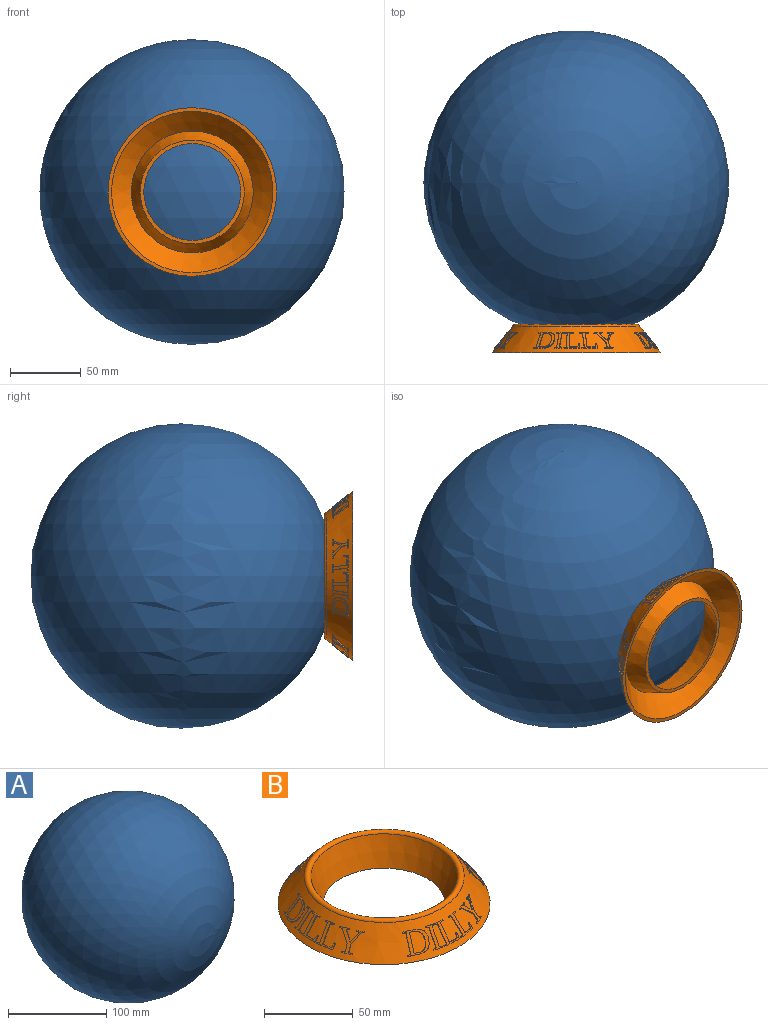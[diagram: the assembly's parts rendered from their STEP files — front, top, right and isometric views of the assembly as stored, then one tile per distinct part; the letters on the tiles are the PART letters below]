
ASSEMBLY  parts=2 mates=1
PART A: 1 faces, bbox 215.9x215.9x215.9 mm
  f0: sphere r=107.95mm, area 146438.5mm2
PART B: 359 faces, bbox 119.7x119.7x20.4 mm
  f0: cone r=34.29mm half-angle=20.4deg, axis (0,0,1), area 4748.7mm2, adj f1,f6
  f1: torus R=43.18mm, axis (0,0,1), area 1338.6mm2, adj f0,f2
  f2: cone r=45.08mm half-angle=37.9deg, axis (0,0,-1), area 6513.8mm2, adj f1,f3,f14,f15,f16,f17,f18,f19
  f3: plane 119.38x119.38mm, normal (0,0,-1), area 932.3mm2, adj f2,f4
  f4: cone r=57.15mm half-angle=44.5deg, axis (0,0,-1), area 6284.1mm2, adj f3,f5
  f5: cone r=36.83mm half-angle=24.1deg, axis (0,0,1), area 3915.4mm2, adj f4,f6
  f6: plane 73.66x73.66mm, normal (0,0,-1), area 567.5mm2, adj f0,f5
  f7: extruded ~4.03x1.55mm, area 2.2mm2, adj f8,f13,f26,f27
  f8: extruded ~4.07x2.56mm, area 2.5mm2, adj f7,f9,f26,f27
  f9: extruded ~3.88x3.58mm, area 2.5mm2, adj f8,f10,f26,f27
  f10: extruded ~3.93x3.1mm, area 2.5mm2, adj f9,f11,f26,f27
  f11: plane 1.87x1.21mm, normal (-0.56,0.25,-0.79), area 1mm2, adj f10,f12,f26,f27
  f12: plane 9.9x7.21mm, normal (-0.41,-0.91,0), area 6.2mm2, adj f11,f13,f26,f27
  f13: extruded ~2.9x1.7mm, area 1.5mm2, adj f7,f12,f26,f27
  f14: plane 1.69x1.4mm, normal (-0.49,0.38,-0.78), area 0.9mm2, adj f2,f15,f25,f26
  f15: plane 10.12x7.39mm, normal (0.41,0.91,0), area 6.3mm2, adj f2,f14,f16,f26
  f16: plane 1.84x1.07mm, normal (0.62,-0.11,0.78), area 0.9mm2, adj f2,f15,f17,f26
  f17: plane 0.75x0.68mm, normal (0.41,0.91,0), area 0.3mm2, adj f2,f16,f18,f26
  f18: plane 1.77x1.23mm, normal (-0.56,0.25,-0.79), area 0.9mm2, adj f2,f17,f19,f26
  f19: plane 4.72x2.66mm, normal (-0.56,0.26,-0.79), area 2.5mm2, adj f2,f18,f20,f26
  f20: extruded ~5.6x1.84mm, area 3mm2, adj f2,f19,f21,f26
  f21: extruded ~4.62x3.21mm, area 2.9mm2, adj f2,f20,f22,f26
  f22: extruded ~4.52x4.16mm, area 2.9mm2, adj f2,f21,f23,f26
  f23: extruded ~5.04x3.83mm, area 3.1mm2, adj f2,f22,f24,f26
  f24: plane 5.98x3.42mm, normal (0.56,-0.25,0.79), area 3.3mm2, adj f2,f23,f25,f26
  f25: plane 0.75x0.68mm, normal (0.41,0.91,0), area 0.3mm2, adj f2,f14,f24,f26
  f26: cone r=45.48mm half-angle=37.9deg, axis (0,0,-1), area 71mm2, adj f7,f8,f9,f10,f11,f12,f13,f14
  f27: cone r=45.08mm half-angle=37.9deg, axis (0,0,-1), area 86.4mm2, adj f7,f8,f9,f10,f11,f12,f13
  f28: plane 0.75x0.73mm, normal (-0.22,-0.98,0), area 0.3mm2, adj f2,f29,f39,f40
  f29: plane 5.66x1.75mm, normal (0.6,-0.14,0.79), area 2.9mm2, adj f2,f28,f30,f40
  f30: plane 0.75x0.73mm, normal (0.22,0.98,0), area 0.3mm2, adj f2,f29,f31,f40
  f31: plane 1.81x1.01mm, normal (-0.56,0.28,-0.78), area 0.9mm2, adj f2,f30,f32,f40
  f32: plane 10.09x7.83mm, normal (0.22,0.98,0), area 6.3mm2, adj f2,f31,f33,f40
  f33: plane 1.89x0.67mm, normal (0.63,0.02,0.78), area 0.9mm2, adj f2,f32,f34,f40
  f34: plane 0.75x0.73mm, normal (0.22,0.98,0), area 0.3mm2, adj f2,f33,f35,f40
  f35: plane 5.65x1.73mm, normal (-0.6,0.14,-0.79), area 2.9mm2, adj f2,f34,f36,f40
  f36: plane 0.75x0.73mm, normal (-0.22,-0.98,0), area 0.3mm2, adj f2,f35,f37,f40
  f37: plane 1.82x0.94mm, normal (0.56,-0.28,0.78), area 0.9mm2, adj f2,f36,f38,f40
  f38: plane 10.09x7.82mm, normal (-0.22,-0.98,0), area 6.3mm2, adj f2,f37,f39,f40
  f39: plane 1.9x0.6mm, normal (-0.63,-0.01,-0.78), area 0.9mm2, adj f2,f28,f38,f40
  f40: cone r=45.48mm half-angle=37.9deg, axis (0,0,-1), area 33.3mm2, adj f28,f29,f30,f31,f32,f33,f34,f35
  f41: plane 6.11x1.03mm, normal (0.61,-0.03,0.79), area 3.1mm2, adj f2,f42,f55,f56
  f42: plane 0.75x0.74mm, normal (-0.05,-1,0), area 0.3mm2, adj f2,f41,f43,f56
  f43: plane 2.21x0.56mm, normal (-0.62,-0.09,-0.78), area 1.1mm2, adj f2,f42,f44,f56
  f44: plane 10.05x7.99mm, normal (-0.05,-1,0), area 6.3mm2, adj f2,f43,f45,f56
  f45: plane 2.8x0.58mm, normal (0.61,-0.03,0.79), area 1.4mm2, adj f2,f44,f46,f56
  f46: extruded ~3.3x0.54mm, area 1.7mm2, adj f2,f45,f47,f56
  f47: plane 2.61x2.21mm, normal (0.18,0.97,0.17), area 1.5mm2, adj f2,f46,f48,f56
  f48: plane 0.7x0.41mm, normal (0.61,-0.03,0.79), area 0.3mm2, adj f2,f47,f49,f56
  f49: plane 3.49x2.9mm, normal (-0.08,-1,-0.04), area 2.1mm2, adj f2,f48,f50,f56
  f50: plane 11.34x1.31mm, normal (-0.61,0.03,-0.79), area 5.6mm2, adj f2,f49,f51,f56
  f51: plane 0.75x0.74mm, normal (0.05,1,0), area 0.3mm2, adj f2,f50,f52,f56
  f52: plane 1.83x0.62mm, normal (0.61,0.12,0.78), area 0.9mm2, adj f2,f51,f53,f56
  f53: plane 10.11x8.06mm, normal (0.05,1,0), area 6.3mm2, adj f2,f52,f54,f56
  f54: plane 1.82x0.78mm, normal (-0.6,0.18,-0.78), area 0.9mm2, adj f2,f53,f55,f56
  f55: plane 0.75x0.75mm, normal (0.05,1,0), area 0.3mm2, adj f2,f41,f54,f56
  f56: cone r=45.48mm half-angle=37.9deg, axis (0,0,-1), area 43.3mm2, adj f41,f42,f43,f44,f45,f46,f47,f48
  f57: plane 0.75x0.74mm, normal (-0.17,0.99,0), area 0.3mm2, adj f2,f58,f71,f72
  f58: plane 1.91x0.45mm, normal (-0.62,0.04,-0.78), area 0.9mm2, adj f2,f57,f59,f72
  f59: plane 10.11x7.95mm, normal (-0.17,0.99,0), area 6.3mm2, adj f2,f58,f60,f72
  f60: plane 1.84x0.79mm, normal (0.57,0.26,0.78), area 0.9mm2, adj f2,f59,f61,f72
  f61: plane 0.75x0.73mm, normal (-0.17,0.99,0), area 0.3mm2, adj f2,f60,f62,f72
  f62: plane 11.26x2.56mm, normal (-0.61,-0.11,-0.79), area 5.6mm2, adj f2,f61,f63,f72
  f63: plane 3.49x2.9mm, normal (0.14,-0.99,-0.04), area 2.1mm2, adj f2,f62,f64,f72
  f64: plane 0.73x0.55mm, normal (0.61,0.11,0.79), area 0.3mm2, adj f2,f63,f65,f72
  f65: plane 2.61x2.32mm, normal (-0.04,0.98,0.17), area 1.5mm2, adj f2,f64,f66,f72
  f66: extruded ~3.29x1.16mm, area 1.7mm2, adj f2,f65,f67,f72
  f67: plane 2.82x0.87mm, normal (0.61,0.11,0.79), area 1.4mm2, adj f2,f66,f68,f72
  f68: plane 10.05x7.88mm, normal (0.17,-0.99,0), area 6.3mm2, adj f2,f67,f69,f72
  f69: plane 2.2x0.92mm, normal (-0.58,-0.23,-0.78), area 1.1mm2, adj f2,f68,f70,f72
  f70: plane 0.75x0.73mm, normal (0.17,-0.99,0), area 0.3mm2, adj f2,f69,f71,f72
  f71: plane 6.13x1.31mm, normal (0.61,0.11,0.79), area 3.1mm2, adj f2,f57,f70,f72
  f72: cone r=45.48mm half-angle=37.9deg, axis (0,0,-1), area 43.3mm2, adj f57,f58,f59,f60,f61,f62,f63,f64
  f73: plane 0.75x0.68mm, normal (0.41,-0.91,0), area 0.3mm2, adj f2,f74,f93,f94
  f74: plane 4.29x2.53mm, normal (0.56,0.25,0.79), area 2.3mm2, adj f2,f73,f75,f94
  f75: plane 0.75x0.68mm, normal (-0.41,0.91,0), area 0.3mm2, adj f2,f74,f76,f94
  f76: plane 1.84x1.01mm, normal (-0.62,-0.11,-0.78), area 0.9mm2, adj f2,f75,f77,f94
  f77: plane 5.83x5.52mm, normal (-0.06,0.91,0.4), area 3.8mm2, adj f2,f76,f78,f94
  f78: plane 5.68x5.53mm, normal (0.64,-0.64,0.42), area 3.9mm2, adj f2,f77,f79,f94
  f79: plane 1.86x1.24mm, normal (-0.5,-0.38,-0.78), area 1mm2, adj f2,f78,f80,f94
  f80: plane 0.75x0.68mm, normal (0.41,-0.91,0), area 0.3mm2, adj f2,f79,f81,f94
  f81: plane 5.86x2.56mm, normal (0.56,0.25,0.79), area 3mm2, adj f2,f80,f82,f94
  f82: plane 0.75x0.68mm, normal (-0.41,0.91,0), area 0.3mm2, adj f2,f81,f83,f94
  f83: plane 1.74x0.74mm, normal (-0.62,-0.09,-0.78), area 0.8mm2, adj f2,f82,f84,f94
  f84: plane 6.97x6.5mm, normal (-0.64,0.64,-0.42), area 4.7mm2, adj f2,f83,f85,f94
  f85: plane 3.97x2.97mm, normal (-0.41,0.91,0), area 2.4mm2, adj f2,f84,f86,f94
  f86: plane 2.17x1.39mm, normal (0.51,0.36,0.78), area 1.1mm2, adj f2,f85,f87,f94
  f87: plane 0.75x0.68mm, normal (-0.41,0.91,0), area 0.3mm2, adj f2,f86,f88,f94
  f88: plane 6.21x3.09mm, normal (-0.56,-0.25,-0.79), area 3.3mm2, adj f2,f87,f89,f94
  f89: plane 0.75x0.68mm, normal (0.41,-0.91,0), area 0.3mm2, adj f2,f88,f90,f94
  f90: plane 2.27x1.17mm, normal (0.61,0.13,0.78), area 1.1mm2, adj f2,f89,f91,f94
  f91: plane 4.02x3mm, normal (0.41,-0.91,0), area 2.4mm2, adj f2,f90,f92,f94
  f92: plane 6.97x6.49mm, normal (0.06,-0.91,-0.41), area 4.6mm2, adj f2,f91,f93,f94
  f93: plane 1.46x1.26mm, normal (-0.48,-0.41,-0.78), area 0.8mm2, adj f2,f73,f92,f94
  f94: cone r=45.48mm half-angle=37.9deg, axis (0,0,-1), area 49.7mm2, adj f73,f74,f75,f76,f77,f78,f79,f80
  f95: extruded ~4.03x1.55mm, area 2.2mm2, adj f96,f101,f114,f115
  f96: extruded ~4.07x2.56mm, area 2.5mm2, adj f95,f97,f114,f115
  f97: extruded ~3.88x3.58mm, area 2.5mm2, adj f96,f98,f114,f115
  f98: extruded ~3.93x3.1mm, area 2.5mm2, adj f97,f99,f114,f115
  f99: plane 1.87x1.21mm, normal (0.25,0.56,-0.79), area 1mm2, adj f98,f100,f114,f115
  f100: plane 9.9x7.21mm, normal (-0.91,0.41,0), area 6.2mm2, adj f99,f101,f114,f115
  f101: extruded ~2.9x1.7mm, area 1.5mm2, adj f95,f100,f114,f115
  f102: plane 1.69x1.4mm, normal (0.38,0.49,-0.78), area 0.9mm2, adj f2,f103,f113,f114
  f103: plane 10.12x7.39mm, normal (0.91,-0.41,0), area 6.3mm2, adj f2,f102,f104,f114
  f104: plane 1.84x1.07mm, normal (-0.11,-0.62,0.78), area 0.9mm2, adj f2,f103,f105,f114
  f105: plane 0.75x0.68mm, normal (0.91,-0.41,0), area 0.3mm2, adj f2,f104,f106,f114
  f106: plane 1.77x1.23mm, normal (0.25,0.56,-0.79), area 0.9mm2, adj f2,f105,f107,f114
  f107: plane 4.72x2.66mm, normal (0.26,0.56,-0.79), area 2.5mm2, adj f2,f106,f108,f114
  f108: extruded ~5.6x1.84mm, area 3mm2, adj f2,f107,f109,f114
  f109: extruded ~4.62x3.21mm, area 2.9mm2, adj f2,f108,f110,f114
  f110: extruded ~4.52x4.16mm, area 2.9mm2, adj f2,f109,f111,f114
  f111: extruded ~5.04x3.83mm, area 3.1mm2, adj f2,f110,f112,f114
  f112: plane 5.98x3.42mm, normal (-0.25,-0.56,0.79), area 3.3mm2, adj f2,f111,f113,f114
  f113: plane 0.75x0.68mm, normal (0.91,-0.41,0), area 0.3mm2, adj f2,f102,f112,f114
  f114: cone r=45.48mm half-angle=37.9deg, axis (0,0,-1), area 71mm2, adj f95,f96,f97,f98,f99,f100,f101,f102
  f115: cone r=45.08mm half-angle=37.9deg, axis (0,0,-1), area 86.4mm2, adj f95,f96,f97,f98,f99,f100,f101
  f116: plane 0.75x0.73mm, normal (-0.98,0.22,0), area 0.3mm2, adj f2,f117,f127,f128
  f117: plane 5.66x1.75mm, normal (-0.14,-0.6,0.79), area 2.9mm2, adj f2,f116,f118,f128
  f118: plane 0.75x0.73mm, normal (0.98,-0.22,0), area 0.3mm2, adj f2,f117,f119,f128
  f119: plane 1.81x1.01mm, normal (0.28,0.56,-0.78), area 0.9mm2, adj f2,f118,f120,f128
  f120: plane 10.09x7.83mm, normal (0.98,-0.22,0), area 6.3mm2, adj f2,f119,f121,f128
  f121: plane 1.89x0.67mm, normal (0.02,-0.63,0.78), area 0.9mm2, adj f2,f120,f122,f128
  f122: plane 0.75x0.73mm, normal (0.98,-0.22,0), area 0.3mm2, adj f2,f121,f123,f128
  f123: plane 5.65x1.73mm, normal (0.14,0.6,-0.79), area 2.9mm2, adj f2,f122,f124,f128
  f124: plane 0.75x0.73mm, normal (-0.98,0.22,0), area 0.3mm2, adj f2,f123,f125,f128
  f125: plane 1.82x0.94mm, normal (-0.28,-0.56,0.78), area 0.9mm2, adj f2,f124,f126,f128
  f126: plane 10.09x7.82mm, normal (-0.98,0.22,0), area 6.3mm2, adj f2,f125,f127,f128
  f127: plane 1.9x0.6mm, normal (-0.01,0.63,-0.78), area 0.9mm2, adj f2,f116,f126,f128
  f128: cone r=45.48mm half-angle=37.9deg, axis (0,0,-1), area 33.3mm2, adj f116,f117,f118,f119,f120,f121,f122,f123
  f129: plane 6.11x1.03mm, normal (-0.03,-0.61,0.79), area 3.1mm2, adj f2,f130,f143,f144
  f130: plane 0.75x0.74mm, normal (-1,0.05,0), area 0.3mm2, adj f2,f129,f131,f144
  f131: plane 2.21x0.56mm, normal (-0.09,0.62,-0.78), area 1.1mm2, adj f2,f130,f132,f144
  f132: plane 10.05x7.99mm, normal (-1,0.05,0), area 6.3mm2, adj f2,f131,f133,f144
  f133: plane 2.8x0.58mm, normal (-0.03,-0.61,0.79), area 1.4mm2, adj f2,f132,f134,f144
  f134: extruded ~3.3x0.54mm, area 1.7mm2, adj f2,f133,f135,f144
  f135: plane 2.61x2.21mm, normal (0.97,-0.18,0.17), area 1.5mm2, adj f2,f134,f136,f144
  f136: plane 0.7x0.41mm, normal (-0.03,-0.61,0.79), area 0.3mm2, adj f2,f135,f137,f144
  f137: plane 3.49x2.9mm, normal (-1,0.08,-0.04), area 2.1mm2, adj f2,f136,f138,f144
  f138: plane 11.34x1.31mm, normal (0.03,0.61,-0.79), area 5.6mm2, adj f2,f137,f139,f144
  f139: plane 0.75x0.74mm, normal (1,-0.05,0), area 0.3mm2, adj f2,f138,f140,f144
  f140: plane 1.83x0.62mm, normal (0.12,-0.61,0.78), area 0.9mm2, adj f2,f139,f141,f144
  f141: plane 10.11x8.06mm, normal (1,-0.05,0), area 6.3mm2, adj f2,f140,f142,f144
  f142: plane 1.82x0.78mm, normal (0.18,0.6,-0.78), area 0.9mm2, adj f2,f141,f143,f144
  f143: plane 0.75x0.75mm, normal (1,-0.05,0), area 0.3mm2, adj f2,f129,f142,f144
  f144: cone r=45.48mm half-angle=37.9deg, axis (0,0,-1), area 43.3mm2, adj f129,f130,f131,f132,f133,f134,f135,f136
  f145: plane 0.75x0.74mm, normal (0.99,0.17,0), area 0.3mm2, adj f2,f146,f159,f160
  f146: plane 1.91x0.45mm, normal (0.04,0.62,-0.78), area 0.9mm2, adj f2,f145,f147,f160
  f147: plane 10.11x7.95mm, normal (0.99,0.17,0), area 6.3mm2, adj f2,f146,f148,f160
  f148: plane 1.84x0.79mm, normal (0.26,-0.57,0.78), area 0.9mm2, adj f2,f147,f149,f160
  f149: plane 0.75x0.73mm, normal (0.99,0.17,0), area 0.3mm2, adj f2,f148,f150,f160
  f150: plane 11.26x2.56mm, normal (-0.11,0.61,-0.79), area 5.6mm2, adj f2,f149,f151,f160
  f151: plane 3.49x2.9mm, normal (-0.99,-0.14,-0.04), area 2.1mm2, adj f2,f150,f152,f160
  f152: plane 0.73x0.55mm, normal (0.11,-0.61,0.79), area 0.3mm2, adj f2,f151,f153,f160
  f153: plane 2.61x2.32mm, normal (0.98,0.04,0.17), area 1.5mm2, adj f2,f152,f154,f160
  f154: extruded ~3.29x1.16mm, area 1.7mm2, adj f2,f153,f155,f160
  f155: plane 2.82x0.87mm, normal (0.11,-0.61,0.79), area 1.4mm2, adj f2,f154,f156,f160
  f156: plane 10.05x7.88mm, normal (-0.99,-0.17,0), area 6.3mm2, adj f2,f155,f157,f160
  f157: plane 2.2x0.92mm, normal (-0.23,0.58,-0.78), area 1.1mm2, adj f2,f156,f158,f160
  f158: plane 0.75x0.73mm, normal (-0.99,-0.17,0), area 0.3mm2, adj f2,f157,f159,f160
  f159: plane 6.13x1.31mm, normal (0.11,-0.61,0.79), area 3.1mm2, adj f2,f145,f158,f160
  f160: cone r=45.48mm half-angle=37.9deg, axis (0,0,-1), area 43.3mm2, adj f145,f146,f147,f148,f149,f150,f151,f152
  f161: plane 0.75x0.68mm, normal (-0.91,-0.41,0), area 0.3mm2, adj f2,f162,f181,f182
  f162: plane 4.29x2.53mm, normal (0.25,-0.56,0.79), area 2.3mm2, adj f2,f161,f163,f182
  f163: plane 0.75x0.68mm, normal (0.91,0.41,0), area 0.3mm2, adj f2,f162,f164,f182
  f164: plane 1.84x1.01mm, normal (-0.11,0.62,-0.78), area 0.9mm2, adj f2,f163,f165,f182
  f165: plane 5.83x5.52mm, normal (0.91,0.06,0.4), area 3.8mm2, adj f2,f164,f166,f182
  f166: plane 5.68x5.53mm, normal (-0.64,-0.64,0.42), area 3.9mm2, adj f2,f165,f167,f182
  f167: plane 1.86x1.24mm, normal (-0.38,0.5,-0.78), area 1mm2, adj f2,f166,f168,f182
  f168: plane 0.75x0.68mm, normal (-0.91,-0.41,0), area 0.3mm2, adj f2,f167,f169,f182
  f169: plane 5.86x2.56mm, normal (0.25,-0.56,0.79), area 3mm2, adj f2,f168,f170,f182
  f170: plane 0.75x0.68mm, normal (0.91,0.41,0), area 0.3mm2, adj f2,f169,f171,f182
  f171: plane 1.74x0.74mm, normal (-0.09,0.62,-0.78), area 0.8mm2, adj f2,f170,f172,f182
  f172: plane 6.97x6.5mm, normal (0.64,0.64,-0.42), area 4.7mm2, adj f2,f171,f173,f182
  f173: plane 3.97x2.97mm, normal (0.91,0.41,0), area 2.4mm2, adj f2,f172,f174,f182
  f174: plane 2.17x1.39mm, normal (0.36,-0.51,0.78), area 1.1mm2, adj f2,f173,f175,f182
  f175: plane 0.75x0.68mm, normal (0.91,0.41,0), area 0.3mm2, adj f2,f174,f176,f182
  f176: plane 6.21x3.09mm, normal (-0.25,0.56,-0.79), area 3.3mm2, adj f2,f175,f177,f182
  f177: plane 0.75x0.68mm, normal (-0.91,-0.41,0), area 0.3mm2, adj f2,f176,f178,f182
  f178: plane 2.27x1.17mm, normal (0.13,-0.61,0.78), area 1.1mm2, adj f2,f177,f179,f182
  f179: plane 4.02x3mm, normal (-0.91,-0.41,0), area 2.4mm2, adj f2,f178,f180,f182
  f180: plane 6.97x6.49mm, normal (-0.91,-0.06,-0.41), area 4.6mm2, adj f2,f179,f181,f182
  f181: plane 1.46x1.26mm, normal (-0.41,0.48,-0.78), area 0.8mm2, adj f2,f161,f180,f182
  f182: cone r=45.48mm half-angle=37.9deg, axis (0,0,-1), area 49.7mm2, adj f161,f162,f163,f164,f165,f166,f167,f168
  f183: extruded ~4.03x1.55mm, area 2.2mm2, adj f184,f189,f202,f203
  f184: extruded ~4.07x2.56mm, area 2.5mm2, adj f183,f185,f202,f203
  f185: extruded ~3.88x3.58mm, area 2.5mm2, adj f184,f186,f202,f203
  f186: extruded ~3.93x3.1mm, area 2.5mm2, adj f185,f187,f202,f203
  f187: plane 1.87x1.21mm, normal (0.56,-0.25,-0.79), area 1mm2, adj f186,f188,f202,f203
  f188: plane 9.9x7.21mm, normal (0.41,0.91,0), area 6.2mm2, adj f187,f189,f202,f203
  f189: extruded ~2.9x1.7mm, area 1.5mm2, adj f183,f188,f202,f203
  f190: plane 1.69x1.4mm, normal (0.49,-0.38,-0.78), area 0.9mm2, adj f2,f191,f201,f202
  f191: plane 10.12x7.39mm, normal (-0.41,-0.91,0), area 6.3mm2, adj f2,f190,f192,f202
  f192: plane 1.84x1.07mm, normal (-0.62,0.11,0.78), area 0.9mm2, adj f2,f191,f193,f202
  f193: plane 0.75x0.68mm, normal (-0.41,-0.91,0), area 0.3mm2, adj f2,f192,f194,f202
  f194: plane 1.77x1.23mm, normal (0.56,-0.25,-0.79), area 0.9mm2, adj f2,f193,f195,f202
  f195: plane 4.72x2.66mm, normal (0.56,-0.26,-0.79), area 2.5mm2, adj f2,f194,f196,f202
  f196: extruded ~5.6x1.84mm, area 3mm2, adj f2,f195,f197,f202
  f197: extruded ~4.62x3.21mm, area 2.9mm2, adj f2,f196,f198,f202
  f198: extruded ~4.52x4.16mm, area 2.9mm2, adj f2,f197,f199,f202
  f199: extruded ~5.04x3.83mm, area 3.1mm2, adj f2,f198,f200,f202
  f200: plane 5.98x3.42mm, normal (-0.56,0.25,0.79), area 3.3mm2, adj f2,f199,f201,f202
  f201: plane 0.75x0.68mm, normal (-0.41,-0.91,0), area 0.3mm2, adj f2,f190,f200,f202
  f202: cone r=45.48mm half-angle=37.9deg, axis (0,0,-1), area 71mm2, adj f183,f184,f185,f186,f187,f188,f189,f190
  f203: cone r=45.08mm half-angle=37.9deg, axis (0,0,-1), area 86.4mm2, adj f183,f184,f185,f186,f187,f188,f189
  f204: plane 0.75x0.73mm, normal (0.22,0.98,0), area 0.3mm2, adj f2,f205,f215,f216
  f205: plane 5.66x1.75mm, normal (-0.6,0.14,0.79), area 2.9mm2, adj f2,f204,f206,f216
  f206: plane 0.75x0.73mm, normal (-0.22,-0.98,0), area 0.3mm2, adj f2,f205,f207,f216
  f207: plane 1.81x1.01mm, normal (0.56,-0.28,-0.78), area 0.9mm2, adj f2,f206,f208,f216
  f208: plane 10.09x7.83mm, normal (-0.22,-0.98,0), area 6.3mm2, adj f2,f207,f209,f216
  f209: plane 1.89x0.67mm, normal (-0.63,-0.02,0.78), area 0.9mm2, adj f2,f208,f210,f216
  f210: plane 0.75x0.73mm, normal (-0.22,-0.98,0), area 0.3mm2, adj f2,f209,f211,f216
  f211: plane 5.65x1.73mm, normal (0.6,-0.14,-0.79), area 2.9mm2, adj f2,f210,f212,f216
  f212: plane 0.75x0.73mm, normal (0.22,0.98,0), area 0.3mm2, adj f2,f211,f213,f216
  f213: plane 1.82x0.94mm, normal (-0.56,0.28,0.78), area 0.9mm2, adj f2,f212,f214,f216
  f214: plane 10.09x7.82mm, normal (0.22,0.98,0), area 6.3mm2, adj f2,f213,f215,f216
  f215: plane 1.9x0.6mm, normal (0.63,0.01,-0.78), area 0.9mm2, adj f2,f204,f214,f216
  f216: cone r=45.48mm half-angle=37.9deg, axis (0,0,-1), area 33.3mm2, adj f204,f205,f206,f207,f208,f209,f210,f211
  f217: plane 6.11x1.03mm, normal (-0.61,0.03,0.79), area 3.1mm2, adj f2,f218,f231,f232
  f218: plane 0.75x0.74mm, normal (0.05,1,0), area 0.3mm2, adj f2,f217,f219,f232
  f219: plane 2.21x0.56mm, normal (0.62,0.09,-0.78), area 1.1mm2, adj f2,f218,f220,f232
  f220: plane 10.05x7.99mm, normal (0.05,1,0), area 6.3mm2, adj f2,f219,f221,f232
  f221: plane 2.8x0.58mm, normal (-0.61,0.03,0.79), area 1.4mm2, adj f2,f220,f222,f232
  f222: extruded ~3.3x0.54mm, area 1.7mm2, adj f2,f221,f223,f232
  f223: plane 2.61x2.21mm, normal (-0.18,-0.97,0.17), area 1.5mm2, adj f2,f222,f224,f232
  f224: plane 0.7x0.41mm, normal (-0.61,0.03,0.79), area 0.3mm2, adj f2,f223,f225,f232
  f225: plane 3.49x2.9mm, normal (0.08,1,-0.04), area 2.1mm2, adj f2,f224,f226,f232
  f226: plane 11.34x1.31mm, normal (0.61,-0.03,-0.79), area 5.6mm2, adj f2,f225,f227,f232
  f227: plane 0.75x0.74mm, normal (-0.05,-1,0), area 0.3mm2, adj f2,f226,f228,f232
  f228: plane 1.83x0.62mm, normal (-0.61,-0.12,0.78), area 0.9mm2, adj f2,f227,f229,f232
  f229: plane 10.11x8.06mm, normal (-0.05,-1,0), area 6.3mm2, adj f2,f228,f230,f232
  f230: plane 1.82x0.78mm, normal (0.6,-0.18,-0.78), area 0.9mm2, adj f2,f229,f231,f232
  f231: plane 0.75x0.75mm, normal (-0.05,-1,0), area 0.3mm2, adj f2,f217,f230,f232
  f232: cone r=45.48mm half-angle=37.9deg, axis (0,0,-1), area 43.3mm2, adj f217,f218,f219,f220,f221,f222,f223,f224
  f233: plane 0.75x0.74mm, normal (0.17,-0.99,0), area 0.3mm2, adj f2,f234,f247,f248
  f234: plane 1.91x0.45mm, normal (0.62,-0.04,-0.78), area 0.9mm2, adj f2,f233,f235,f248
  f235: plane 10.11x7.95mm, normal (0.17,-0.99,0), area 6.3mm2, adj f2,f234,f236,f248
  f236: plane 1.84x0.79mm, normal (-0.57,-0.26,0.78), area 0.9mm2, adj f2,f235,f237,f248
  f237: plane 0.75x0.73mm, normal (0.17,-0.99,0), area 0.3mm2, adj f2,f236,f238,f248
  f238: plane 11.26x2.56mm, normal (0.61,0.11,-0.79), area 5.6mm2, adj f2,f237,f239,f248
  f239: plane 3.49x2.9mm, normal (-0.14,0.99,-0.04), area 2.1mm2, adj f2,f238,f240,f248
  f240: plane 0.73x0.55mm, normal (-0.61,-0.11,0.79), area 0.3mm2, adj f2,f239,f241,f248
  f241: plane 2.61x2.32mm, normal (0.04,-0.98,0.17), area 1.5mm2, adj f2,f240,f242,f248
  f242: extruded ~3.29x1.16mm, area 1.7mm2, adj f2,f241,f243,f248
  f243: plane 2.82x0.87mm, normal (-0.61,-0.11,0.79), area 1.4mm2, adj f2,f242,f244,f248
  f244: plane 10.05x7.88mm, normal (-0.17,0.99,0), area 6.3mm2, adj f2,f243,f245,f248
  f245: plane 2.2x0.92mm, normal (0.58,0.23,-0.78), area 1.1mm2, adj f2,f244,f246,f248
  f246: plane 0.75x0.73mm, normal (-0.17,0.99,0), area 0.3mm2, adj f2,f245,f247,f248
  f247: plane 6.13x1.31mm, normal (-0.61,-0.11,0.79), area 3.1mm2, adj f2,f233,f246,f248
  f248: cone r=45.48mm half-angle=37.9deg, axis (0,0,-1), area 43.3mm2, adj f233,f234,f235,f236,f237,f238,f239,f240
  f249: plane 0.75x0.68mm, normal (-0.41,0.91,0), area 0.3mm2, adj f2,f250,f269,f270
  f250: plane 4.29x2.53mm, normal (-0.56,-0.25,0.79), area 2.3mm2, adj f2,f249,f251,f270
  f251: plane 0.75x0.68mm, normal (0.41,-0.91,0), area 0.3mm2, adj f2,f250,f252,f270
  f252: plane 1.84x1.01mm, normal (0.62,0.11,-0.78), area 0.9mm2, adj f2,f251,f253,f270
  f253: plane 5.83x5.52mm, normal (0.06,-0.91,0.4), area 3.8mm2, adj f2,f252,f254,f270
  f254: plane 5.68x5.53mm, normal (-0.64,0.64,0.42), area 3.9mm2, adj f2,f253,f255,f270
  f255: plane 1.86x1.24mm, normal (0.5,0.38,-0.78), area 1mm2, adj f2,f254,f256,f270
  f256: plane 0.75x0.68mm, normal (-0.41,0.91,0), area 0.3mm2, adj f2,f255,f257,f270
  f257: plane 5.86x2.56mm, normal (-0.56,-0.25,0.79), area 3mm2, adj f2,f256,f258,f270
  f258: plane 0.75x0.68mm, normal (0.41,-0.91,0), area 0.3mm2, adj f2,f257,f259,f270
  f259: plane 1.74x0.74mm, normal (0.62,0.09,-0.78), area 0.8mm2, adj f2,f258,f260,f270
  f260: plane 6.97x6.5mm, normal (0.64,-0.64,-0.42), area 4.7mm2, adj f2,f259,f261,f270
  f261: plane 3.97x2.97mm, normal (0.41,-0.91,0), area 2.4mm2, adj f2,f260,f262,f270
  f262: plane 2.17x1.39mm, normal (-0.51,-0.36,0.78), area 1.1mm2, adj f2,f261,f263,f270
  f263: plane 0.75x0.68mm, normal (0.41,-0.91,0), area 0.3mm2, adj f2,f262,f264,f270
  f264: plane 6.21x3.09mm, normal (0.56,0.25,-0.79), area 3.3mm2, adj f2,f263,f265,f270
  f265: plane 0.75x0.68mm, normal (-0.41,0.91,0), area 0.3mm2, adj f2,f264,f266,f270
  f266: plane 2.27x1.17mm, normal (-0.61,-0.13,0.78), area 1.1mm2, adj f2,f265,f267,f270
  f267: plane 4.02x3mm, normal (-0.41,0.91,0), area 2.4mm2, adj f2,f266,f268,f270
  f268: plane 6.97x6.49mm, normal (-0.06,0.91,-0.41), area 4.6mm2, adj f2,f267,f269,f270
  f269: plane 1.46x1.26mm, normal (0.48,0.41,-0.78), area 0.8mm2, adj f2,f249,f268,f270
  f270: cone r=45.48mm half-angle=37.9deg, axis (0,0,-1), area 49.7mm2, adj f249,f250,f251,f252,f253,f254,f255,f256
  f271: extruded ~4.03x1.55mm, area 2.2mm2, adj f272,f277,f290,f291
  f272: extruded ~4.07x2.56mm, area 2.5mm2, adj f271,f273,f290,f291
  f273: extruded ~3.88x3.58mm, area 2.5mm2, adj f272,f274,f290,f291
  f274: extruded ~3.93x3.1mm, area 2.5mm2, adj f273,f275,f290,f291
  f275: plane 1.87x1.21mm, normal (-0.25,-0.56,-0.79), area 1mm2, adj f274,f276,f290,f291
  f276: plane 9.9x7.21mm, normal (0.91,-0.41,0), area 6.2mm2, adj f275,f277,f290,f291
  f277: extruded ~2.9x1.7mm, area 1.5mm2, adj f271,f276,f290,f291
  f278: plane 1.69x1.4mm, normal (-0.38,-0.49,-0.78), area 0.9mm2, adj f2,f279,f289,f290
  f279: plane 10.12x7.39mm, normal (-0.91,0.41,0), area 6.3mm2, adj f2,f278,f280,f290
  f280: plane 1.84x1.07mm, normal (0.11,0.62,0.78), area 0.9mm2, adj f2,f279,f281,f290
  f281: plane 0.75x0.68mm, normal (-0.91,0.41,0), area 0.3mm2, adj f2,f280,f282,f290
  f282: plane 1.77x1.23mm, normal (-0.25,-0.56,-0.79), area 0.9mm2, adj f2,f281,f283,f290
  f283: plane 4.72x2.66mm, normal (-0.26,-0.56,-0.79), area 2.5mm2, adj f2,f282,f284,f290
  f284: extruded ~5.6x1.84mm, area 3mm2, adj f2,f283,f285,f290
  f285: extruded ~4.62x3.21mm, area 2.9mm2, adj f2,f284,f286,f290
  f286: extruded ~4.52x4.16mm, area 2.9mm2, adj f2,f285,f287,f290
  f287: extruded ~5.04x3.83mm, area 3.1mm2, adj f2,f286,f288,f290
  f288: plane 5.98x3.42mm, normal (0.25,0.56,0.79), area 3.3mm2, adj f2,f287,f289,f290
  f289: plane 0.75x0.68mm, normal (-0.91,0.41,0), area 0.3mm2, adj f2,f278,f288,f290
  f290: cone r=45.48mm half-angle=37.9deg, axis (0,0,-1), area 71mm2, adj f271,f272,f273,f274,f275,f276,f277,f278
  f291: cone r=45.08mm half-angle=37.9deg, axis (0,0,-1), area 86.4mm2, adj f271,f272,f273,f274,f275,f276,f277
  f292: plane 0.75x0.73mm, normal (0.98,-0.22,0), area 0.3mm2, adj f2,f293,f303,f304
  f293: plane 5.66x1.75mm, normal (0.14,0.6,0.79), area 2.9mm2, adj f2,f292,f294,f304
  f294: plane 0.75x0.73mm, normal (-0.98,0.22,0), area 0.3mm2, adj f2,f293,f295,f304
  f295: plane 1.81x1.01mm, normal (-0.28,-0.56,-0.78), area 0.9mm2, adj f2,f294,f296,f304
  f296: plane 10.09x7.83mm, normal (-0.98,0.22,0), area 6.3mm2, adj f2,f295,f297,f304
  f297: plane 1.89x0.67mm, normal (-0.02,0.63,0.78), area 0.9mm2, adj f2,f296,f298,f304
  f298: plane 0.75x0.73mm, normal (-0.98,0.22,0), area 0.3mm2, adj f2,f297,f299,f304
  f299: plane 5.65x1.73mm, normal (-0.14,-0.6,-0.79), area 2.9mm2, adj f2,f298,f300,f304
  f300: plane 0.75x0.73mm, normal (0.98,-0.22,0), area 0.3mm2, adj f2,f299,f301,f304
  f301: plane 1.82x0.94mm, normal (0.28,0.56,0.78), area 0.9mm2, adj f2,f300,f302,f304
  f302: plane 10.09x7.82mm, normal (0.98,-0.22,0), area 6.3mm2, adj f2,f301,f303,f304
  f303: plane 1.9x0.6mm, normal (0.01,-0.63,-0.78), area 0.9mm2, adj f2,f292,f302,f304
  f304: cone r=45.48mm half-angle=37.9deg, axis (0,0,-1), area 33.3mm2, adj f292,f293,f294,f295,f296,f297,f298,f299
  f305: plane 6.11x1.03mm, normal (0.03,0.61,0.79), area 3.1mm2, adj f2,f306,f319,f320
  f306: plane 0.75x0.74mm, normal (1,-0.05,0), area 0.3mm2, adj f2,f305,f307,f320
  f307: plane 2.21x0.56mm, normal (0.09,-0.62,-0.78), area 1.1mm2, adj f2,f306,f308,f320
  f308: plane 10.05x7.99mm, normal (1,-0.05,0), area 6.3mm2, adj f2,f307,f309,f320
  f309: plane 2.8x0.58mm, normal (0.03,0.61,0.79), area 1.4mm2, adj f2,f308,f310,f320
  f310: extruded ~3.3x0.54mm, area 1.7mm2, adj f2,f309,f311,f320
  f311: plane 2.61x2.21mm, normal (-0.97,0.18,0.17), area 1.5mm2, adj f2,f310,f312,f320
  f312: plane 0.7x0.41mm, normal (0.03,0.61,0.79), area 0.3mm2, adj f2,f311,f313,f320
  f313: plane 3.49x2.9mm, normal (1,-0.08,-0.04), area 2.1mm2, adj f2,f312,f314,f320
  f314: plane 11.34x1.31mm, normal (-0.03,-0.61,-0.79), area 5.6mm2, adj f2,f313,f315,f320
  f315: plane 0.75x0.74mm, normal (-1,0.05,0), area 0.3mm2, adj f2,f314,f316,f320
  f316: plane 1.83x0.62mm, normal (-0.12,0.61,0.78), area 0.9mm2, adj f2,f315,f317,f320
  f317: plane 10.11x8.06mm, normal (-1,0.05,0), area 6.3mm2, adj f2,f316,f318,f320
  f318: plane 1.82x0.78mm, normal (-0.18,-0.6,-0.78), area 0.9mm2, adj f2,f317,f319,f320
  f319: plane 0.75x0.75mm, normal (-1,0.05,0), area 0.3mm2, adj f2,f305,f318,f320
  f320: cone r=45.48mm half-angle=37.9deg, axis (0,0,-1), area 43.3mm2, adj f305,f306,f307,f308,f309,f310,f311,f312
  f321: plane 0.75x0.74mm, normal (-0.99,-0.17,0), area 0.3mm2, adj f2,f322,f335,f336
  f322: plane 1.91x0.45mm, normal (-0.04,-0.62,-0.78), area 0.9mm2, adj f2,f321,f323,f336
  f323: plane 10.11x7.95mm, normal (-0.99,-0.17,0), area 6.3mm2, adj f2,f322,f324,f336
  f324: plane 1.84x0.79mm, normal (-0.26,0.57,0.78), area 0.9mm2, adj f2,f323,f325,f336
  f325: plane 0.75x0.73mm, normal (-0.99,-0.17,0), area 0.3mm2, adj f2,f324,f326,f336
  f326: plane 11.26x2.56mm, normal (0.11,-0.61,-0.79), area 5.6mm2, adj f2,f325,f327,f336
  f327: plane 3.49x2.9mm, normal (0.99,0.14,-0.04), area 2.1mm2, adj f2,f326,f328,f336
  f328: plane 0.73x0.55mm, normal (-0.11,0.61,0.79), area 0.3mm2, adj f2,f327,f329,f336
  f329: plane 2.61x2.32mm, normal (-0.98,-0.04,0.17), area 1.5mm2, adj f2,f328,f330,f336
  f330: extruded ~3.29x1.16mm, area 1.7mm2, adj f2,f329,f331,f336
  f331: plane 2.82x0.87mm, normal (-0.11,0.61,0.79), area 1.4mm2, adj f2,f330,f332,f336
  f332: plane 10.05x7.88mm, normal (0.99,0.17,0), area 6.3mm2, adj f2,f331,f333,f336
  f333: plane 2.2x0.92mm, normal (0.23,-0.58,-0.78), area 1.1mm2, adj f2,f332,f334,f336
  f334: plane 0.75x0.73mm, normal (0.99,0.17,0), area 0.3mm2, adj f2,f333,f335,f336
  f335: plane 6.13x1.31mm, normal (-0.11,0.61,0.79), area 3.1mm2, adj f2,f321,f334,f336
  f336: cone r=45.48mm half-angle=37.9deg, axis (0,0,-1), area 43.3mm2, adj f321,f322,f323,f324,f325,f326,f327,f328
  f337: plane 0.75x0.68mm, normal (0.91,0.41,0), area 0.3mm2, adj f2,f338,f357,f358
  f338: plane 4.29x2.53mm, normal (-0.25,0.56,0.79), area 2.3mm2, adj f2,f337,f339,f358
  f339: plane 0.75x0.68mm, normal (-0.91,-0.41,0), area 0.3mm2, adj f2,f338,f340,f358
  f340: plane 1.84x1.01mm, normal (0.11,-0.62,-0.78), area 0.9mm2, adj f2,f339,f341,f358
  f341: plane 5.83x5.52mm, normal (-0.91,-0.06,0.4), area 3.8mm2, adj f2,f340,f342,f358
  f342: plane 5.68x5.53mm, normal (0.64,0.64,0.42), area 3.9mm2, adj f2,f341,f343,f358
  f343: plane 1.86x1.24mm, normal (0.38,-0.5,-0.78), area 1mm2, adj f2,f342,f344,f358
  f344: plane 0.75x0.68mm, normal (0.91,0.41,0), area 0.3mm2, adj f2,f343,f345,f358
  f345: plane 5.86x2.56mm, normal (-0.25,0.56,0.79), area 3mm2, adj f2,f344,f346,f358
  f346: plane 0.75x0.68mm, normal (-0.91,-0.41,0), area 0.3mm2, adj f2,f345,f347,f358
  f347: plane 1.74x0.74mm, normal (0.09,-0.62,-0.78), area 0.8mm2, adj f2,f346,f348,f358
  f348: plane 6.97x6.5mm, normal (-0.64,-0.64,-0.42), area 4.7mm2, adj f2,f347,f349,f358
  f349: plane 3.97x2.97mm, normal (-0.91,-0.41,0), area 2.4mm2, adj f2,f348,f350,f358
  f350: plane 2.17x1.39mm, normal (-0.36,0.51,0.78), area 1.1mm2, adj f2,f349,f351,f358
  f351: plane 0.75x0.68mm, normal (-0.91,-0.41,0), area 0.3mm2, adj f2,f350,f352,f358
  f352: plane 6.21x3.09mm, normal (0.25,-0.56,-0.79), area 3.3mm2, adj f2,f351,f353,f358
  f353: plane 0.75x0.68mm, normal (0.91,0.41,0), area 0.3mm2, adj f2,f352,f354,f358
  f354: plane 2.27x1.17mm, normal (-0.13,0.61,0.78), area 1.1mm2, adj f2,f353,f355,f358
  f355: plane 4.02x3mm, normal (0.91,0.41,0), area 2.4mm2, adj f2,f354,f356,f358
  f356: plane 6.97x6.49mm, normal (0.91,0.06,-0.41), area 4.6mm2, adj f2,f355,f357,f358
  f357: plane 1.46x1.26mm, normal (0.41,-0.48,-0.78), area 0.8mm2, adj f2,f337,f356,f358
  f358: cone r=45.48mm half-angle=37.9deg, axis (0,0,-1), area 49.7mm2, adj f337,f338,f339,f340,f341,f342,f343,f344
PLACE A rot(axis=(0,0.71,0.71),180deg) t=(0,0,0)mm
PLACE B rot(axis=(-1,0,0),90deg) t=(-34.29,-112.45,0)mm
MATE slider B.f0 <-> A.f0  axis (0,1,0) through (0,-101.58,0)mm
